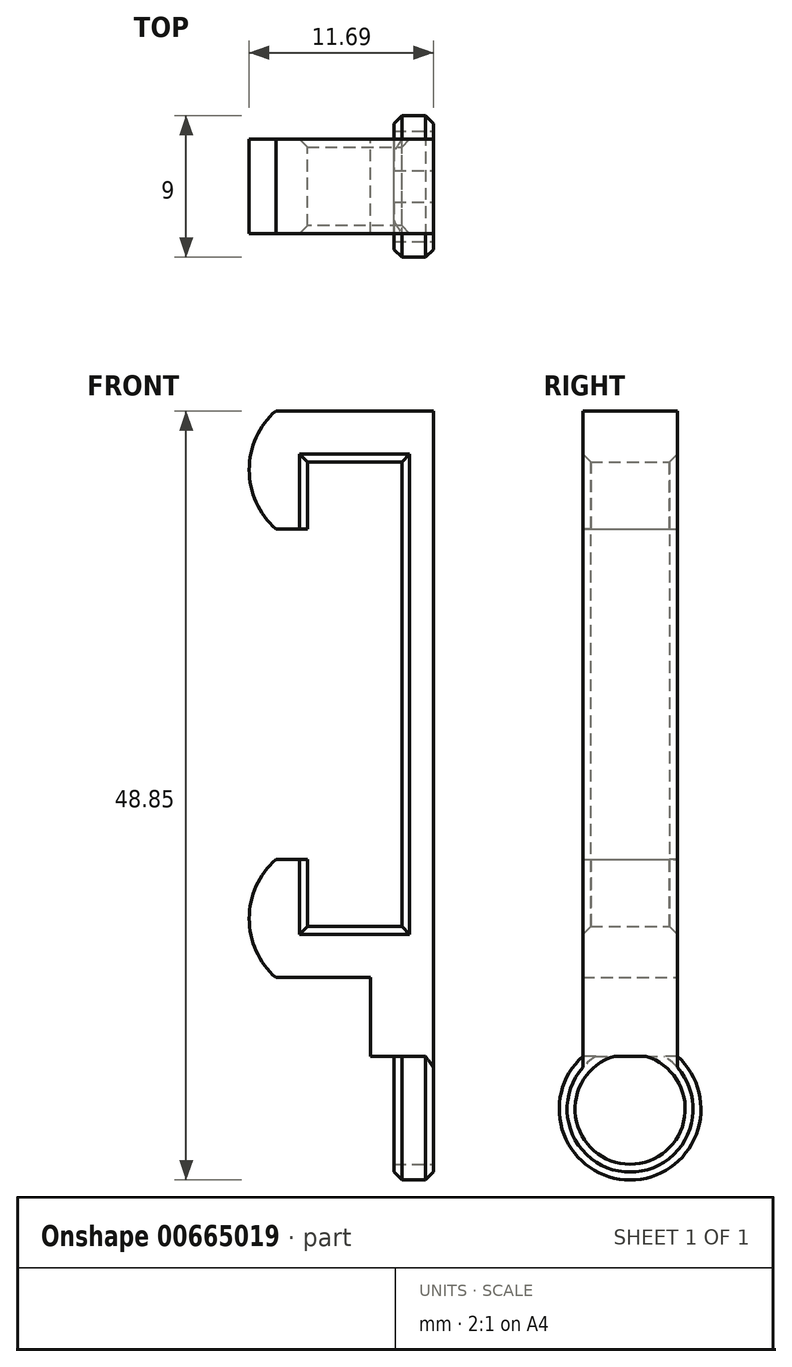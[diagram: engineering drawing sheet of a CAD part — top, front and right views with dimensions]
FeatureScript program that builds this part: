
annotation { "Feature Type Name" : "Feature", "Feature Type Description" : "" }
export const myFeature = defineFeature(function(context is Context, id is Id, definition is map)
    precondition{}
    {
        {
            var Q0;
            Q0=qCreatedBy(makeId("Front.planeOp"),FACE);
            var sketch = newSketch(context, id + "F0", { "sketchPlane" : qUnion([Q0])});
            skLineSegment(sketch, "E0", {"start": v(10, 0) * mm, "end": v(10, 36) * mm});
            skLineSegment(sketch, "E1", {"start": v(10, 36) * mm, "end": v(0, 36) * mm});
            skLineSegment(sketch, "E2", {"start": v(0, 36) * mm, "end": v(0, 28.5) * mm});
            skLineSegment(sketch, "E3", {"start": v(0, 28.5) * mm, "end": v(2, 28.5) * mm});
            skLineSegment(sketch, "E4", {"start": v(2, 28.5) * mm, "end": v(2, 32.75) * mm});
            skLineSegment(sketch, "E5", {"start": v(2, 32.75) * mm, "end": v(8, 32.75) * mm});
            skLineSegment(sketch, "E6", {"start": v(8, 32.75) * mm, "end": v(8, 3.25) * mm});
            skLineSegment(sketch, "E7", {"start": v(8, 3.25) * mm, "end": v(2, 3.25) * mm});
            skLineSegment(sketch, "E8", {"start": v(2, 3.25) * mm, "end": v(2, 7.5) * mm});
            skLineSegment(sketch, "E9", {"start": v(2, 7.5) * mm, "end": v(0, 7.5) * mm});
            skLineSegment(sketch, "E10", {"start": v(0, 7.5) * mm, "end": v(0, 0) * mm});
            skLineSegment(sketch, "E11", {"start": v(0, 0) * mm, "end": v(10, 0) * mm});
            skArc(sketch, "E12", {"start": v(0, 36) * mm, "mid": v(-1.7, 32.25) * mm, "end": v(0, 28.5) * mm});
            skArc(sketch, "E13", {"start": v(0, 7.5) * mm, "mid": v(-1.7, 3.75) * mm, "end": v(0, 0) * mm});
            skLineSegment(sketch, "E14", {"start": v(10, 0) * mm, "end": v(10, -5) * mm});
            skLineSegment(sketch, "E15", {"start": v(10, -5) * mm, "end": v(6, -5) * mm});
            skLineSegment(sketch, "E16", {"start": v(6, -5) * mm, "end": v(6, 0) * mm});
            skSolve(sketch);
        }
        {
            var Q0;
            {var subQ0=sQuery(id+"F0.wireOp",EDGE,"E0");Q0=makeQuery(id+"F0.imprint","IMPRINT",FACE,{"disambiguationData":[TD([[makeQuery(id+"F0.imprint","IMPRINT",EDGE,{"derivedFrom":subQ0}),1.0]])]});}
            var Q1;
            Q1=makeQuery(id+"F0.imprint","IMPRINT",FACE,{"disambiguationData":[TD([[makeQuery(id+"F0.imprint","IMPRINT",EDGE,{"derivedFrom":sQuery(id+"F0.wireOp",EDGE,"E10")}),-1.0]])]});
            var Q2;
            Q2=makeQuery(id+"F0.imprint","IMPRINT",FACE,{"disambiguationData":[TD([[makeQuery(id+"F0.imprint","IMPRINT",EDGE,{"derivedFrom":sQuery(id+"F0.wireOp",EDGE,"E2")}),-1.0]])]});
            var Q3;
            {var subQ0=sQuery(id+"F0.wireOp",EDGE,"E14");Q3=makeQuery(id+"F0.imprint","IMPRINT",FACE,{"disambiguationData":[TD([[makeQuery(id+"F0.imprint","IMPRINT",EDGE,{"derivedFrom":subQ0}),-1.0]])]});}
            extrude(context, id + "F1", {"entities" : qUnion([Q0, Q1, Q2, Q3]), "endBound" : BoundingType.SYMMETRIC, "depth" : 6 * mm, "offsetDistance" : 25 * mm});
        }
        {
            var Q0;
            Q0=makeQuery(id+"F1.opExtrude","SWEPT_FACE",FACE,{"disambiguationData":[OSD([sQuery(id+"F0.wireOp",EDGE,"E0"),sQuery(id+"F0.wireOp",EDGE,"E14")])]});
            var sketch = newSketch(context, id + "F2", { "sketchPlane" : qUnion([Q0])});
            skCircle(sketch, "E17", {"center": v(0, -8.35) * mm, "radius": 4.5 * mm});
            skCircle(sketch, "E18", {"center": v(0, -8.35) * mm, "radius": 3.5 * mm});
            skSolve(sketch);
        }
        {
            var Q0;
            {var subQ1=sQuery(id+"F0.wireOp",EDGE,"E14");var subQ3=makeQuery(id+"F1.opExtrude","SWEPT_EDGE",EDGE,{"disambiguationData":[OSD([subQ1,sQuery(id+"F0.wireOp",EDGE,"E15")])]});var subQ6=sQuery(id+"F2.wireOp",EDGE,"E18");var subQ7=makeQuery(id+"F2.imprint","INTERSECT",VERTEX,{"disambiguationData":[OD(0.0)],"derivedFrom":[subQ3,subQ6]});Q0=makeQuery(id+"F2.imprint","IMPRINT",FACE,{"disambiguationData":[TD([[makeQuery(id+"F2.imprint","IMPRINT",EDGE,{"disambiguationData":[TD([[subQ7,1.0]])],"derivedFrom":subQ6}),-1.0]])]});}
            extrude(context, id + "F3", {"entities" : qUnion([Q0]), "operationType" : NewBodyOperationType.ADD, "oppositeDirection" : true, "depth" : 2.5 * mm, "offsetDistance" : 25 * mm});
        }
        {
            var Q0;
            Q0=makeQuery(id+"F3.opExtrude","CAP_EDGE",EDGE,{"disambiguationData":[OSD([sQuery(id+"F2.wireOp",EDGE,"E17")])],"isStart":false});
            chamfer(context, id + "F4", {"entities" : qUnion([Q0]), "width" : .5 * mm, "tangentPropagation" : true});
        }
        {
            var Q0;
            Q0=makeQuery(id+"F3.opExtrude","CAP_EDGE",EDGE,{"disambiguationData":[OSD([sQuery(id+"F2.wireOp",EDGE,"E17")])],"isStart":true});
            chamfer(context, id + "F5", {"entities" : qUnion([Q0]), "width" : .5 * mm, "tangentPropagation" : true});
        }
        {
            var Q0;
            Q0=makeQuery(id+"F1.opExtrude","CAP_EDGE",EDGE,{"disambiguationData":[OSD([sQuery(id+"F0.wireOp",EDGE,"E8")])],"isStart":false});
            var Q1;
            Q1=makeQuery(id+"F1.opExtrude","CAP_EDGE",EDGE,{"disambiguationData":[OSD([sQuery(id+"F0.wireOp",EDGE,"E7")])],"isStart":false});
            var Q2;
            Q2=makeQuery(id+"F1.opExtrude","CAP_EDGE",EDGE,{"disambiguationData":[OSD([sQuery(id+"F0.wireOp",EDGE,"E6")])],"isStart":false});
            var Q3;
            Q3=makeQuery(id+"F1.opExtrude","CAP_EDGE",EDGE,{"disambiguationData":[OSD([sQuery(id+"F0.wireOp",EDGE,"E4")])],"isStart":false});
            var Q4;
            Q4=makeQuery(id+"F1.opExtrude","CAP_EDGE",EDGE,{"disambiguationData":[OSD([sQuery(id+"F0.wireOp",EDGE,"E5")])],"isStart":false});
            var Q5;
            Q5=makeQuery(id+"F1.opExtrude","CAP_EDGE",EDGE,{"disambiguationData":[OSD([sQuery(id+"F0.wireOp",EDGE,"E8")])],"isStart":true});
            var Q6;
            Q6=makeQuery(id+"F1.opExtrude","CAP_EDGE",EDGE,{"disambiguationData":[OSD([sQuery(id+"F0.wireOp",EDGE,"E7")])],"isStart":true});
            var Q7;
            Q7=makeQuery(id+"F1.opExtrude","CAP_EDGE",EDGE,{"disambiguationData":[OSD([sQuery(id+"F0.wireOp",EDGE,"E6")])],"isStart":true});
            var Q8;
            Q8=makeQuery(id+"F1.opExtrude","CAP_EDGE",EDGE,{"disambiguationData":[OSD([sQuery(id+"F0.wireOp",EDGE,"E5")])],"isStart":true});
            var Q9;
            Q9=makeQuery(id+"F1.opExtrude","CAP_EDGE",EDGE,{"disambiguationData":[OSD([sQuery(id+"F0.wireOp",EDGE,"E4")])],"isStart":true});
            chamfer(context, id + "F6", {"entities" : qUnion([Q0, Q1, Q2, Q3, Q4, Q5, Q6, Q7, Q8, Q9]), "width" : .5 * mm, "tangentPropagation" : true});
        }
    });
